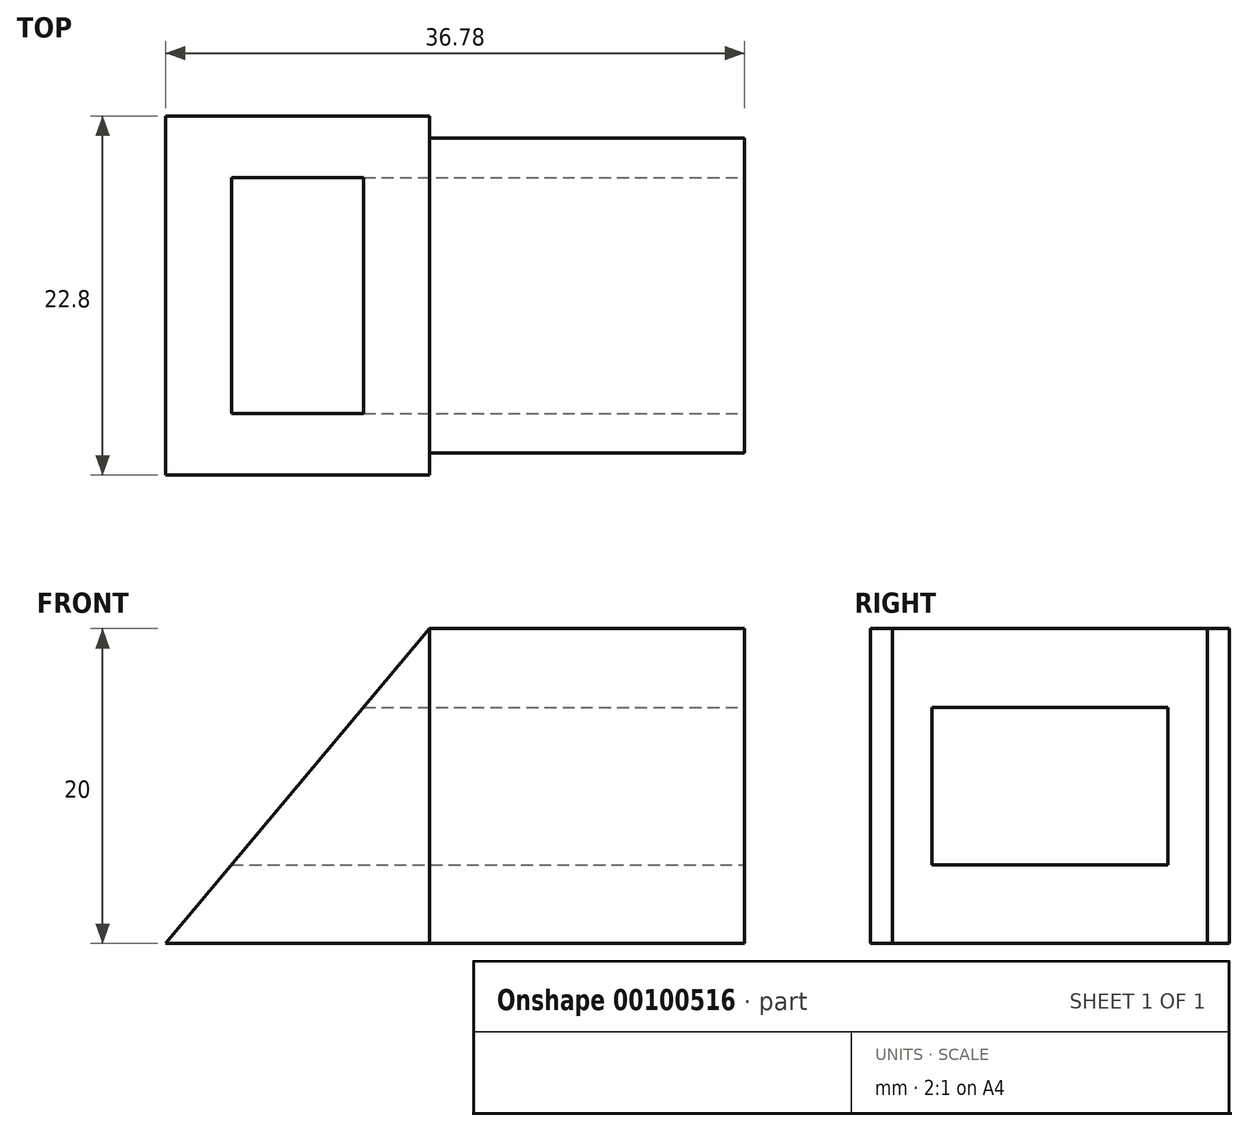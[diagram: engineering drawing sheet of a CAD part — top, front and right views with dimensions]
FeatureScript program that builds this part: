
annotation { "Feature Type Name" : "Feature", "Feature Type Description" : "" }
export const myFeature = defineFeature(function(context is Context, id is Id, definition is map)
    precondition{}
    {
        {
            var Q0;
            Q0=qCreatedBy(makeId("Front.planeOp"),FACE);
            var sketch = newSketch(context, id + "F0", { "sketchPlane" : qUnion([Q0])});
            skLineSegment(sketch, "E0", {"start": v(0, 0) * mm, "end": v(20, 0) * mm});
            skLineSegment(sketch, "E1", {"start": v(20, 0) * mm, "end": v(20, 20) * mm});
            skLineSegment(sketch, "E2", {"start": v(20, 20) * mm, "end": v(0, 20) * mm});
            skLineSegment(sketch, "E3", {"start": v(0, 20) * mm, "end": v(-16.78, 0) * mm});
            skLineSegment(sketch, "E4", {"start": v(-16.78, 0) * mm, "end": v(0, 0) * mm});
            skLineSegment(sketch, "E5", {"start": v(0, 20) * mm, "end": v(0, 0) * mm});
            skSolve(sketch);
        }
        {
            var Q0;
            Q0 = qSketchRegion(id + "F0", true);
            extrude(context, id + "F1", {"entities" : qUnion([Q0]), "depth" : 20 * mm});
        }
        {
            var Q0;
            Q0=makeQuery(id+"F0.imprint","IMPRINT",FACE,{"disambiguationData":[TD([[makeQuery(id+"F0.imprint","IMPRINT",EDGE,{"derivedFrom":sQuery(id+"F0.wireOp",EDGE,"E3")}),1.0]])]});
            extrude(context, id + "F2", {"entities" : qUnion([Q0]), "operationType" : NewBodyOperationType.ADD, "depth" : 21.4 * mm, "hasSecondDirection" : true, "secondDirectionOppositeDirection" : true, "secondDirectionDepth" : 1.4 * mm});
        }
        {
            var Q0;
            Q0=makeQuery(id+"F1.opExtrude","SWEPT_FACE",FACE,{"disambiguationData":[OSD([sQuery(id+"F0.wireOp",EDGE,"E1")])]});
            var sketch = newSketch(context, id + "F3", { "sketchPlane" : qUnion([Q0])});
            skPoint(sketch, "E6.centerSnap0", {"position": v(-10, 20) * mm});
            skPoint(sketch, "E6.centerSnap1", {"position": v(0, 10) * mm});
            skLineSegment(sketch, "E7.bottom", {"start": v(-2.5, 15) * mm, "end": v(-17.5, 15) * mm});
            skLineSegment(sketch, "E7.top", {"start": v(-2.5, 5) * mm, "end": v(-17.5, 5) * mm});
            skLineSegment(sketch, "E7.left", {"start": v(-2.5, 15) * mm, "end": v(-2.5, 5) * mm});
            skLineSegment(sketch, "E7.right", {"start": v(-17.5, 15) * mm, "end": v(-17.5, 5) * mm});
            skPoint(sketch, "E7.middle", {"position": v(-10, 10) * mm});
            skSolve(sketch);
        }
        {
            var Q0;
            Q0 = qSketchRegion(id + "F3", true);
            extrude(context, id + "F4", {"entities" : qUnion([Q0]), "operationType" : NewBodyOperationType.REMOVE, "endBound" : BoundingType.THROUGH_ALL, "oppositeDirection" : true, "depth" : 25 * mm});
        }
    });
